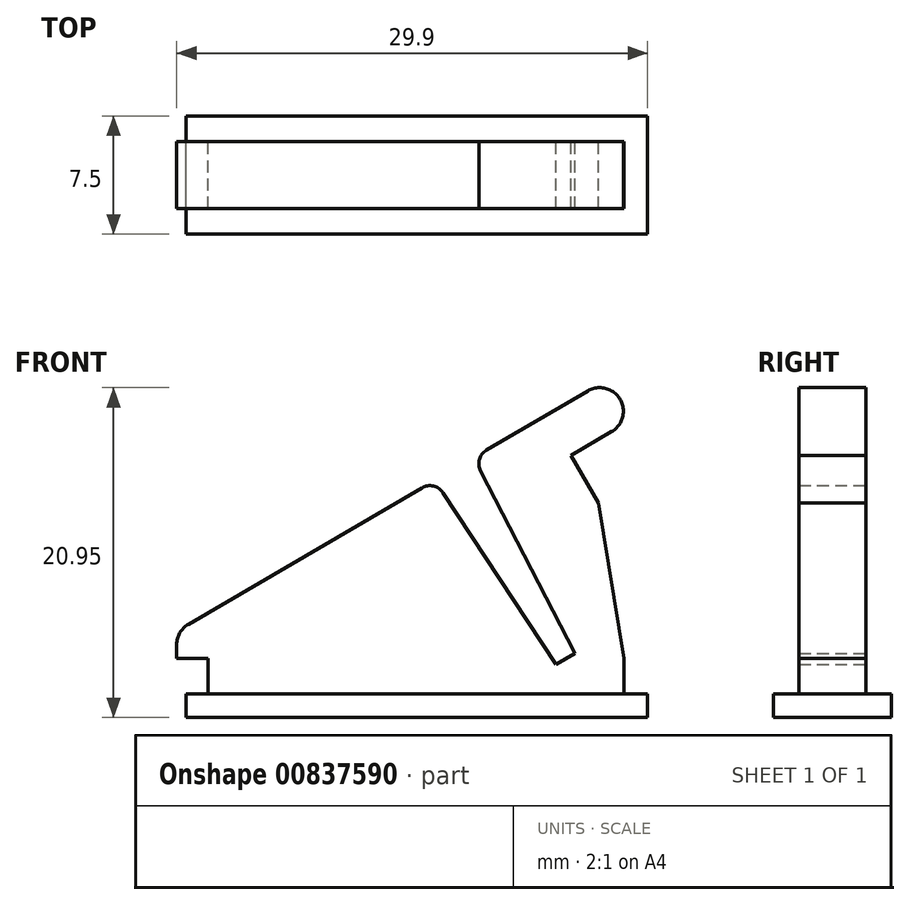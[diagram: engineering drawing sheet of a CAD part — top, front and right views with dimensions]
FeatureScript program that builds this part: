
annotation { "Feature Type Name" : "Feature", "Feature Type Description" : "" }
export const myFeature = defineFeature(function(context is Context, id is Id, definition is map)
    precondition{}
    {
        {
            var Q0;
            Q0=qCreatedBy(makeId("Front.planeOp"),FACE);
            var sketch = newSketch(context, id + "F0", { "sketchPlane" : qUnion([Q0])});
            skLineSegment(sketch, "E0", {"start": v(-14.61, 0) * mm, "end": v(14.69, 0) * mm});
            skLineSegment(sketch, "E1", {"start": v(14.69, 0) * mm, "end": v(14.69, 1.5) * mm});
            skLineSegment(sketch, "E2", {"start": v(14.69, 1.5) * mm, "end": v(13.19, 1.5) * mm});
            skLineSegment(sketch, "E3", {"start": v(13.19, 1.5) * mm, "end": v(13.19, 3.75) * mm});
            skLineSegment(sketch, "E4", {"start": v(-13.21, 3.75) * mm, "end": v(-13.21, 1.5) * mm});
            skLineSegment(sketch, "E5", {"start": v(-13.21, 1.5) * mm, "end": v(-14.61, 1.5) * mm});
            skLineSegment(sketch, "E6", {"start": v(-14.61, 1.5) * mm, "end": v(-14.61, 0) * mm});
            skLineSegment(sketch, "E7", {"start": v(-13.21, 3.75) * mm, "end": v(-15.21, 3.75) * mm});
            skLineSegment(sketch, "E8", {"start": v(-15.21, 3.75) * mm, "end": v(-15.21, 4.62) * mm});
            skLineSegment(sketch, "E9", {"start": v(12.96, 20.2) * mm, "end": v(12.96, 20.2) * mm});
            skLineSegment(sketch, "E10", {"start": v(12.42, 18.15) * mm, "end": v(9.83, 16.64) * mm});
            skLineSegment(sketch, "E11", {"start": v(9.83, 16.64) * mm, "end": v(11.6, 13.62) * mm});
            skLineSegment(sketch, "E12", {"start": v(11.6, 13.62) * mm, "end": v(13.19, 3.75) * mm});
            skPoint(sketch, "E13.visualSharp", {"position": v(12.2, 21.5) * mm});
            skArc(sketch, "E13.filletArc", {"start": v(12.96, 20.2) * mm, "mid": v(12.04, 20.9) * mm, "end": v(10.9, 20.74) * mm});
            skPoint(sketch, "E14.visualSharp", {"position": v(13.71, 18.9) * mm});
            skArc(sketch, "E14.filletArc", {"start": v(12.42, 18.15) * mm, "mid": v(13.11, 19.07) * mm, "end": v(12.96, 20.2) * mm});
            skPoint(sketch, "E15.visualSharp", {"position": v(-15.21, 5.48) * mm});
            skArc(sketch, "E15.filletArc", {"start": v(-14.47, 5.91) * mm, "mid": v(-15.01, 5.37) * mm, "end": v(-15.21, 4.62) * mm});
            skLineSegment(sketch, "E16", {"start": v(1.71, 14.27) * mm, "end": v(8.88, 3.37) * mm});
            skLineSegment(sketch, "E17", {"start": v(8.88, 3.37) * mm, "end": v(10.07, 4.06) * mm});
            skLineSegment(sketch, "E18", {"start": v(10.07, 4.06) * mm, "end": v(4.09, 15.66) * mm});
            skLineSegment(sketch, "E19", {"start": v(4.47, 16.98) * mm, "end": v(10.9, 20.74) * mm});
            skLineSegment(sketch, "E20", {"start": v(-14.47, 5.91) * mm, "end": v(0.37, 14.59) * mm});
            skPoint(sketch, "E21.visualSharp", {"position": v(1.2, 15.07) * mm});
            skArc(sketch, "E21.filletArc", {"start": v(1.71, 14.27) * mm, "mid": v(1.1, 14.7) * mm, "end": v(0.37, 14.59) * mm});
            skPoint(sketch, "E22.visualSharp", {"position": v(3.65, 16.5) * mm});
            skArc(sketch, "E22.filletArc", {"start": v(4.47, 16.98) * mm, "mid": v(4.01, 16.4) * mm, "end": v(4.09, 15.66) * mm});
            skLineSegment(sketch, "E23", {"start": v(-13.21, 1.5) * mm, "end": v(13.19, 1.5) * mm});
            skSolve(sketch);
        }
        {
            var Q0;
            Q0=makeQuery(id+"F0.imprint","IMPRINT",FACE,{"disambiguationData":[TD([[makeQuery(id+"F0.imprint","IMPRINT",EDGE,{"derivedFrom":sQuery(id+"F0.wireOp",EDGE,"E0")}),1.0]])]});
            extrude(context, id + "F1", {"entities" : qUnion([Q0]), "endBound" : BoundingType.SYMMETRIC, "depth" : 7.5 * mm, "offsetDistance" : 25 * mm});
        }
        {
            var Q0;
            Q0=makeQuery(id+"F0.imprint","IMPRINT",FACE,{"disambiguationData":[TD([[makeQuery(id+"F0.imprint","IMPRINT",EDGE,{"derivedFrom":sQuery(id+"F0.wireOp",EDGE,"E3")}),1.0]])]});
            extrude(context, id + "F2", {"entities" : qUnion([Q0]), "operationType" : NewBodyOperationType.ADD, "endBound" : BoundingType.SYMMETRIC, "depth" : 4.25 * mm, "offsetDistance" : 25 * mm});
        }
    });
